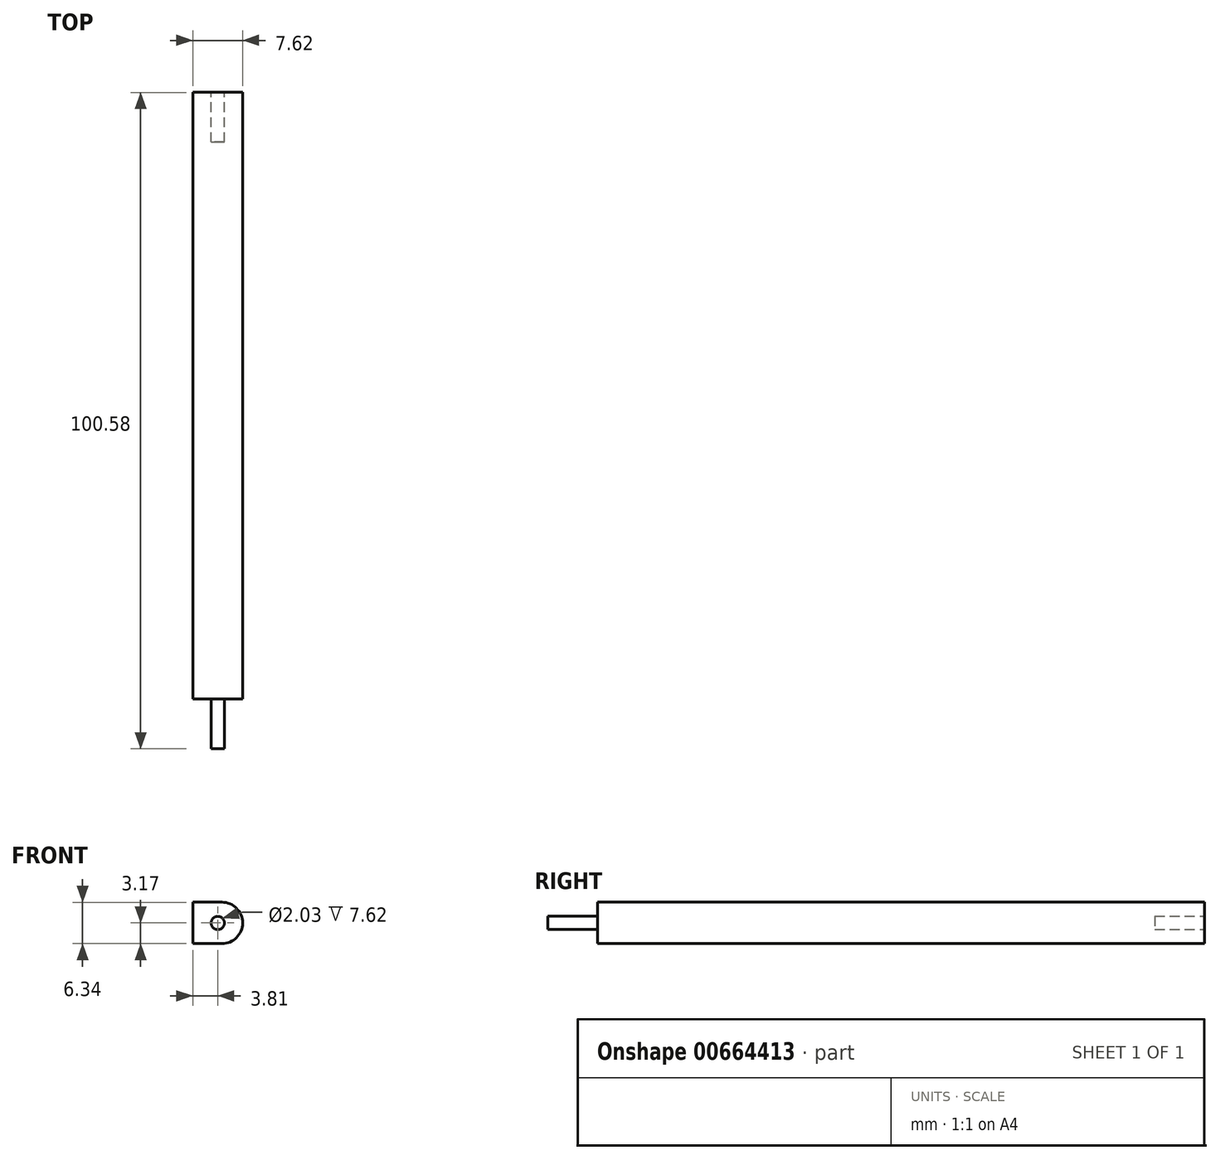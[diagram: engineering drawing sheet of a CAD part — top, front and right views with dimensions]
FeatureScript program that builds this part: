
annotation { "Feature Type Name" : "Feature", "Feature Type Description" : "" }
export const myFeature = defineFeature(function(context is Context, id is Id, definition is map)
    precondition{}
    {
        {
            var Q0;
            Q0=qCreatedBy(makeId("Right.planeOp"),FACE);
            var sketch = newSketch(context, id + "F0", { "sketchPlane" : qUnion([Q0])});
            skLineSegment(sketch, "E0", {"start": v(50.3, 3.18) * mm, "end": v(50.3, -3.17) * mm});
            skLineSegment(sketch, "E1", {"start": v(50.3, -3.17) * mm, "end": v(-50.3, -3.17) * mm});
            skLineSegment(sketch, "E2", {"start": v(-50.3, -3.18) * mm, "end": v(-50.3, 3.18) * mm});
            skLineSegment(sketch, "E3", {"start": v(50.3, 3.18) * mm, "end": v(-50.3, 3.18) * mm});
            skLineSegment(sketch, "E4", {"start": v(0, 0) * mm, "end": v(0, 3.18) * mm});
            skSolve(sketch);
        }
        {
            var Q0;
            Q0 = qSketchRegion(id + "F0", true);
            extrude(context, id + "F1", {"entities" : qUnion([Q0]), "depth" : 7.62 * mm, "offsetDistance" : 25.4 * mm});
        }
        {
            var Q0;
            Q0=makeQuery(id+"F1.opExtrude","CAP_EDGE",EDGE,{"disambiguationData":[OSD([sQuery(id+"F0.wireOp",EDGE,"E1")])],"isStart":false});
            var Q1;
            Q1=makeQuery(id+"F1.opExtrude","CAP_EDGE",EDGE,{"disambiguationData":[OSD([sQuery(id+"F0.wireOp",EDGE,"E3")])],"isStart":false});
            fillet(context, id + "F2", {"entities" : qUnion([Q0, Q1]), "radius" : 3.17 * mm, "tangentPropagation" : true, "allowEdgeOverflow" : false});
        }
        {
            var Q0;
            Q0=makeQuery(id+"F1.opExtrude","SWEPT_FACE",FACE,{"disambiguationData":[OSD([sQuery(id+"F0.wireOp",EDGE,"E0")])]});
            var sketch = newSketch(context, id + "F3", { "sketchPlane" : qUnion([Q0])});
            skLineSegment(sketch, "E5", {"start": v(0, 0) * mm, "end": v(-3.81, 0) * mm});
            skCircle(sketch, "E6", {"center": v(-3.81, 0) * mm, "radius": 1.02 * mm});
            skSolve(sketch);
        }
        {
            var Q0;
            Q0=makeQuery(id+"F1.opExtrude","SWEPT_FACE",FACE,{"disambiguationData":[OSD([sQuery(id+"F0.wireOp",EDGE,"E2")])]});
            var sketch = newSketch(context, id + "F4", { "sketchPlane" : qUnion([Q0])});
            skCircle(sketch, "E7.0", {"center": v(3.81, 0) * mm, "radius": 1.02 * mm});
            skSolve(sketch);
        }
        {
            var Q0;
            Q0=makeQuery(id+"F4.imprint","IMPRINT",FACE,{"disambiguationData":[TD([[makeQuery(id+"F4.imprint","IMPRINT",EDGE,{"derivedFrom":sQuery(id+"F4.wireOp",EDGE,"E7.0")}),-1.0]])]});
            extrude(context, id + "F5", {"entities" : qUnion([Q0]), "operationType" : NewBodyOperationType.REMOVE, "oppositeDirection" : true, "depth" : 7.62 * mm, "offsetDistance" : 25.4 * mm});
        }
        {
            var Q0;
            Q0=makeQuery(id+"F3.imprint","IMPRINT",FACE,{"disambiguationData":[TD([[makeQuery(id+"F3.imprint","IMPRINT",EDGE,{"derivedFrom":sQuery(id+"F3.wireOp",EDGE,"E6")}),1.0]])]});
            extrude(context, id + "F6", {"entities" : qUnion([Q0]), "operationType" : NewBodyOperationType.REMOVE, "oppositeDirection" : true, "depth" : 7.62 * mm, "offsetDistance" : 25.4 * mm});
        }
    });
